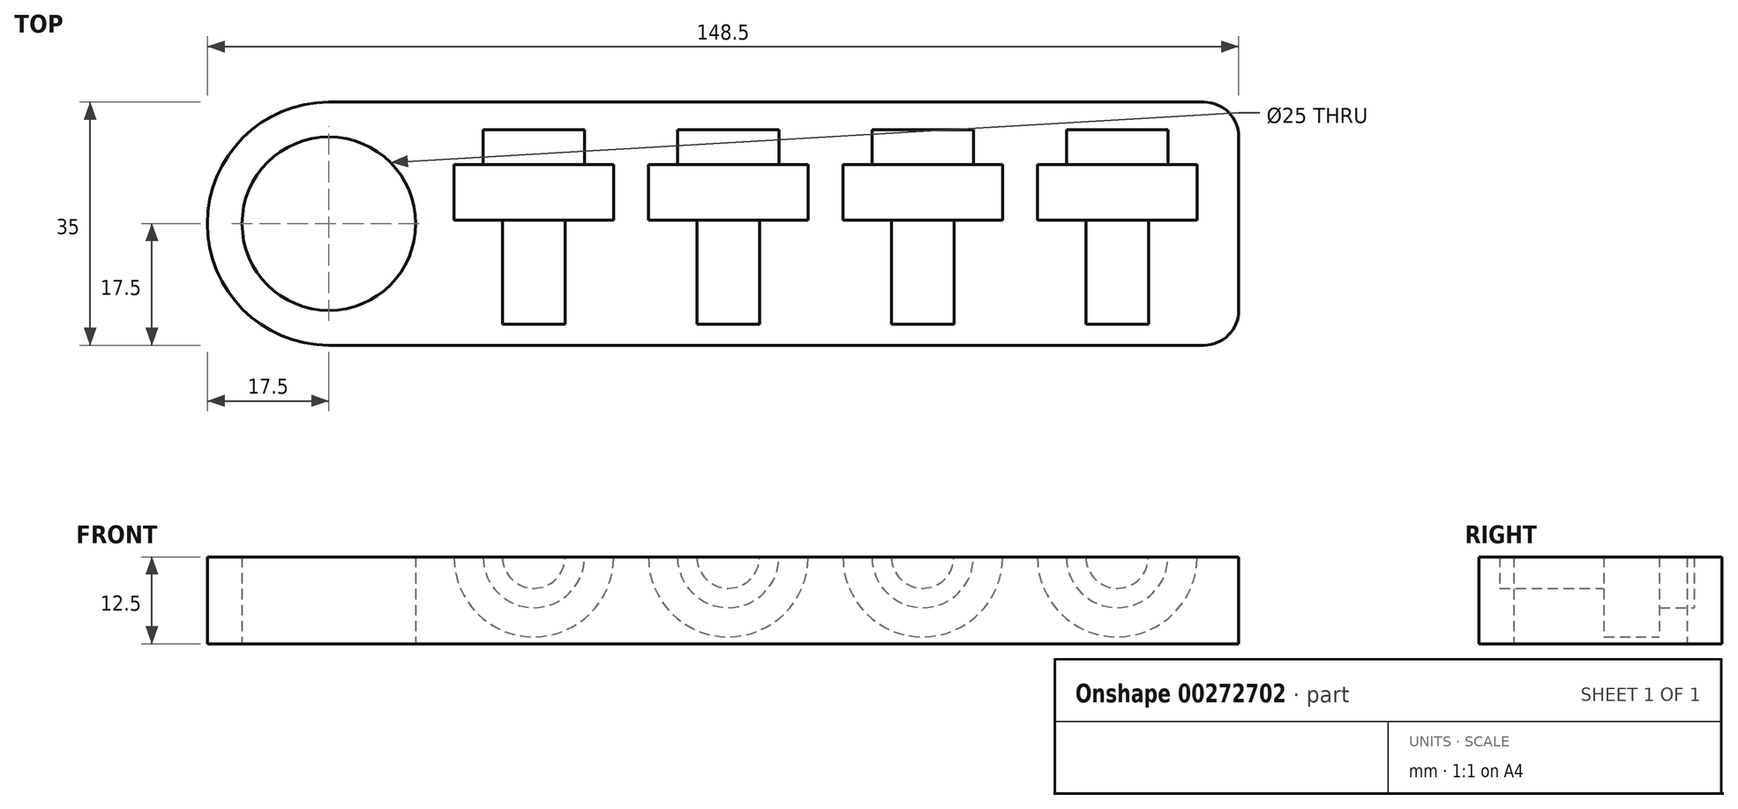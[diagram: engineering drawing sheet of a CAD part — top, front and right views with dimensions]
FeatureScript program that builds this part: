
annotation { "Feature Type Name" : "Feature", "Feature Type Description" : "" }
export const myFeature = defineFeature(function(context is Context, id is Id, definition is map)
    precondition{}
    {
        {
            var Q0;
            Q0=qCreatedBy(makeId("Top.planeOp"),FACE);
            var sketch = newSketch(context, id + "F0", { "sketchPlane" : qUnion([Q0])});
            skLineSegment(sketch, "E0.bottom", {"start": v(17.5, 0) * mm, "end": v(143.5, 0) * mm});
            skLineSegment(sketch, "E0.top", {"start": v(17.5, 35) * mm, "end": v(143.5, 35) * mm});
            skLineSegment(sketch, "E0.left", {"start": v(0, 17.5) * mm, "end": v(0, 17.5) * mm});
            skLineSegment(sketch, "E0.right", {"start": v(148.5, 5) * mm, "end": v(148.5, 30) * mm});
            skLineSegment(sketch, "E1.bottom", {"start": v(0, 0) * mm, "end": v(17.5, 0) * mm, "construction": true});
            skLineSegment(sketch, "E1.top", {"start": v(0, 17.5) * mm, "end": v(17.5, 17.5) * mm, "construction": true});
            skLineSegment(sketch, "E1.left", {"start": v(0, 0) * mm, "end": v(0, 17.5) * mm, "construction": true});
            skLineSegment(sketch, "E1.right", {"start": v(17.5, 0) * mm, "end": v(17.5, 17.5) * mm, "construction": true});
            skCircle(sketch, "E2", {"center": v(17.5, 17.5) * mm, "radius": 12.5 * mm});
            skPoint(sketch, "E3.visualSharp", {"position": v(0, 0) * mm});
            skArc(sketch, "E3.filletArc", {"start": v(0, 17.5) * mm, "mid": v(5.13, 5.13) * mm, "end": v(17.5, 0) * mm});
            skPoint(sketch, "E4.visualSharp", {"position": v(0, 35) * mm});
            skArc(sketch, "E4.filletArc", {"start": v(17.5, 35) * mm, "mid": v(5.13, 29.87) * mm, "end": v(0, 17.5) * mm});
            skPoint(sketch, "E5.visualSharp", {"position": v(148.5, 35) * mm});
            skArc(sketch, "E5.filletArc", {"start": v(148.5, 30) * mm, "mid": v(147.04, 33.54) * mm, "end": v(143.5, 35) * mm});
            skPoint(sketch, "E6.visualSharp", {"position": v(148.5, 0) * mm});
            skArc(sketch, "E6.filletArc", {"start": v(143.5, 0) * mm, "mid": v(147.04, 1.46) * mm, "end": v(148.5, 5) * mm});
            skSolve(sketch);
        }
        {
            var Q0;
            Q0=makeQuery(id+"F0.imprint","IMPRINT",FACE,{"disambiguationData":[TD([[makeQuery(id+"F0.imprint","IMPRINT",EDGE,{"derivedFrom":sQuery(id+"F0.wireOp",EDGE,"E0.bottom")}),1.0]])]});
            extrude(context, id + "F1", {"entities" : qUnion([Q0]), "depth" : 12.5 * mm});
        }
        {
            var Q0;
            Q0=makeQuery(id+"F1.opExtrude","CAP_FACE",FACE,{"disambiguationData":[OSD([sQuery(id+"F0.wireOp",EDGE,"E0.bottom"),sQuery(id+"F0.wireOp",EDGE,"E0.top"),sQuery(id+"F0.wireOp",EDGE,"E0.right"),sQuery(id+"F0.wireOp",EDGE,"E2"),sQuery(id+"F0.wireOp",EDGE,"E3.filletArc"),sQuery(id+"F0.wireOp",EDGE,"E4.filletArc"),sQuery(id+"F0.wireOp",EDGE,"E5.filletArc"),sQuery(id+"F0.wireOp",EDGE,"E6.filletArc")])],"isStart":false});
            var sketch = newSketch(context, id + "F2", { "sketchPlane" : qUnion([Q0])});
            skLineSegment(sketch, "E7.bottom", {"start": v(0, 0) * mm, "end": v(47, 0) * mm, "construction": true});
            skLineSegment(sketch, "E7.top", {"start": v(0, 3) * mm, "end": v(47, 3) * mm, "construction": true});
            skLineSegment(sketch, "E7.left", {"start": v(0, 0) * mm, "end": v(0, 3) * mm, "construction": true});
            skLineSegment(sketch, "E7.right", {"start": v(47, 0) * mm, "end": v(47, 3) * mm, "construction": true});
            skLineSegment(sketch, "E8", {"start": v(47, 3) * mm, "end": v(75, 3) * mm, "construction": true});
            skLineSegment(sketch, "E9", {"start": v(75, 3) * mm, "end": v(103, 3) * mm, "construction": true});
            skLineSegment(sketch, "E10", {"start": v(103, 3) * mm, "end": v(131, 3) * mm, "construction": true});
            skLineSegment(sketch, "E11.bottom", {"start": v(47, 3) * mm, "end": v(51.5, 3) * mm});
            skLineSegment(sketch, "E11.left", {"start": v(47, 3) * mm, "end": v(47, 18) * mm});
            skLineSegment(sketch, "E11.right", {"start": v(51.5, 3) * mm, "end": v(51.5, 18) * mm});
            skLineSegment(sketch, "E12.bottom", {"start": v(75, 3) * mm, "end": v(79.5, 3) * mm});
            skLineSegment(sketch, "E12.left", {"start": v(75, 3) * mm, "end": v(75, 18) * mm});
            skLineSegment(sketch, "E12.right", {"start": v(79.5, 3) * mm, "end": v(79.5, 18) * mm});
            skLineSegment(sketch, "E13.bottom", {"start": v(103, 3) * mm, "end": v(107.5, 3) * mm});
            skLineSegment(sketch, "E13.left", {"start": v(103, 3) * mm, "end": v(103, 18) * mm});
            skLineSegment(sketch, "E13.right", {"start": v(107.5, 3) * mm, "end": v(107.5, 18) * mm});
            skLineSegment(sketch, "E14.bottom", {"start": v(131, 3) * mm, "end": v(135.5, 3) * mm});
            skLineSegment(sketch, "E14.left", {"start": v(131, 3) * mm, "end": v(131, 18) * mm});
            skLineSegment(sketch, "E14.right", {"start": v(135.5, 3) * mm, "end": v(135.5, 18) * mm});
            skLineSegment(sketch, "E15.bottom", {"start": v(51.5, 18) * mm, "end": v(58.5, 18) * mm});
            skLineSegment(sketch, "E15.top", {"start": v(54.3, 26) * mm, "end": v(58.5, 26) * mm});
            skLineSegment(sketch, "E15.left", {"start": v(47, 18) * mm, "end": v(47, 26) * mm});
            skLineSegment(sketch, "E15.right", {"start": v(58.5, 18) * mm, "end": v(58.5, 26) * mm});
            skLineSegment(sketch, "E16.bottom", {"start": v(79.5, 18) * mm, "end": v(86.5, 18) * mm});
            skLineSegment(sketch, "E16.top", {"start": v(82.3, 26) * mm, "end": v(86.5, 26) * mm});
            skLineSegment(sketch, "E16.left", {"start": v(75, 18) * mm, "end": v(75, 26) * mm});
            skLineSegment(sketch, "E16.right", {"start": v(86.5, 18) * mm, "end": v(86.5, 26) * mm});
            skLineSegment(sketch, "E17.bottom", {"start": v(107.5, 18) * mm, "end": v(114.5, 18) * mm});
            skLineSegment(sketch, "E17.top", {"start": v(110.3, 26) * mm, "end": v(114.5, 26) * mm});
            skLineSegment(sketch, "E17.left", {"start": v(103, 18) * mm, "end": v(103, 26) * mm});
            skLineSegment(sketch, "E17.right", {"start": v(114.5, 18) * mm, "end": v(114.5, 26) * mm});
            skLineSegment(sketch, "E18.bottom", {"start": v(135.5, 18) * mm, "end": v(142.5, 18) * mm});
            skLineSegment(sketch, "E18.top", {"start": v(138.3, 26) * mm, "end": v(142.5, 26) * mm});
            skLineSegment(sketch, "E18.left", {"start": v(131, 18) * mm, "end": v(131, 26) * mm});
            skLineSegment(sketch, "E18.right", {"start": v(142.5, 18) * mm, "end": v(142.5, 26) * mm});
            skLineSegment(sketch, "E19.top", {"start": v(131, 31) * mm, "end": v(138.3, 31) * mm});
            skLineSegment(sketch, "E19.left", {"start": v(131, 26) * mm, "end": v(131, 31) * mm});
            skLineSegment(sketch, "E19.right", {"start": v(138.3, 26) * mm, "end": v(138.3, 31) * mm});
            skLineSegment(sketch, "E20.top", {"start": v(103, 31) * mm, "end": v(110.3, 31) * mm});
            skLineSegment(sketch, "E20.left", {"start": v(103, 26) * mm, "end": v(103, 31) * mm});
            skLineSegment(sketch, "E20.right", {"start": v(110.3, 26) * mm, "end": v(110.3, 31) * mm});
            skLineSegment(sketch, "E21.top", {"start": v(75, 31) * mm, "end": v(82.3, 31) * mm});
            skLineSegment(sketch, "E21.left", {"start": v(75, 26) * mm, "end": v(75, 31) * mm});
            skLineSegment(sketch, "E21.right", {"start": v(82.3, 26) * mm, "end": v(82.3, 31) * mm});
            skLineSegment(sketch, "E22.top", {"start": v(47, 31) * mm, "end": v(54.3, 31) * mm});
            skLineSegment(sketch, "E22.left", {"start": v(47, 26) * mm, "end": v(47, 31) * mm});
            skLineSegment(sketch, "E22.right", {"start": v(54.3, 26) * mm, "end": v(54.3, 31) * mm});
            skSolve(sketch);
        }
        {
            var Q0;
            Q0=makeQuery(id+"F2.imprint","IMPRINT",FACE,{"disambiguationData":[TD([[makeQuery(id+"F2.imprint","IMPRINT",EDGE,{"derivedFrom":sQuery(id+"F2.wireOp",EDGE,"E11.bottom")}),1.0]])]});
            var Q1;
            Q1=sQuery(id+"F2.wireOp",EDGE,"E11.left");
            revolve(context, id + "F3", {"operationType" : NewBodyOperationType.REMOVE, "entities" : qUnion([Q0]), "axis" : qUnion([Q1]), "revolveType" : RevolveType.FULL, "oppositeDirection" : true});
        }
        {
            var Q0;
            Q0=makeQuery(id+"F2.imprint","IMPRINT",FACE,{"disambiguationData":[TD([[makeQuery(id+"F2.imprint","IMPRINT",EDGE,{"derivedFrom":sQuery(id+"F2.wireOp",EDGE,"E12.bottom")}),1.0]])]});
            var Q1;
            Q1=sQuery(id+"F2.wireOp",EDGE,"E16.left");
            revolve(context, id + "F4", {"operationType" : NewBodyOperationType.REMOVE, "entities" : qUnion([Q0]), "axis" : qUnion([Q1]), "revolveType" : RevolveType.FULL, "oppositeDirection" : true});
        }
        {
            var Q0;
            Q0=makeQuery(id+"F2.imprint","IMPRINT",FACE,{"disambiguationData":[TD([[makeQuery(id+"F2.imprint","IMPRINT",EDGE,{"derivedFrom":sQuery(id+"F2.wireOp",EDGE,"E13.bottom")}),1.0]])]});
            var Q1;
            Q1=sQuery(id+"F2.wireOp",EDGE,"E17.left");
            revolve(context, id + "F5", {"operationType" : NewBodyOperationType.REMOVE, "entities" : qUnion([Q0]), "axis" : qUnion([Q1]), "revolveType" : RevolveType.FULL, "oppositeDirection" : true});
        }
        {
            var Q0;
            Q0=makeQuery(id+"F2.imprint","IMPRINT",FACE,{"disambiguationData":[TD([[makeQuery(id+"F2.imprint","IMPRINT",EDGE,{"derivedFrom":sQuery(id+"F2.wireOp",EDGE,"E14.bottom")}),1.0]])]});
            var Q1;
            Q1=sQuery(id+"F2.wireOp",EDGE,"E18.left");
            revolve(context, id + "F6", {"operationType" : NewBodyOperationType.REMOVE, "entities" : qUnion([Q0]), "axis" : qUnion([Q1]), "revolveType" : RevolveType.FULL, "oppositeDirection" : true});
        }
    });
